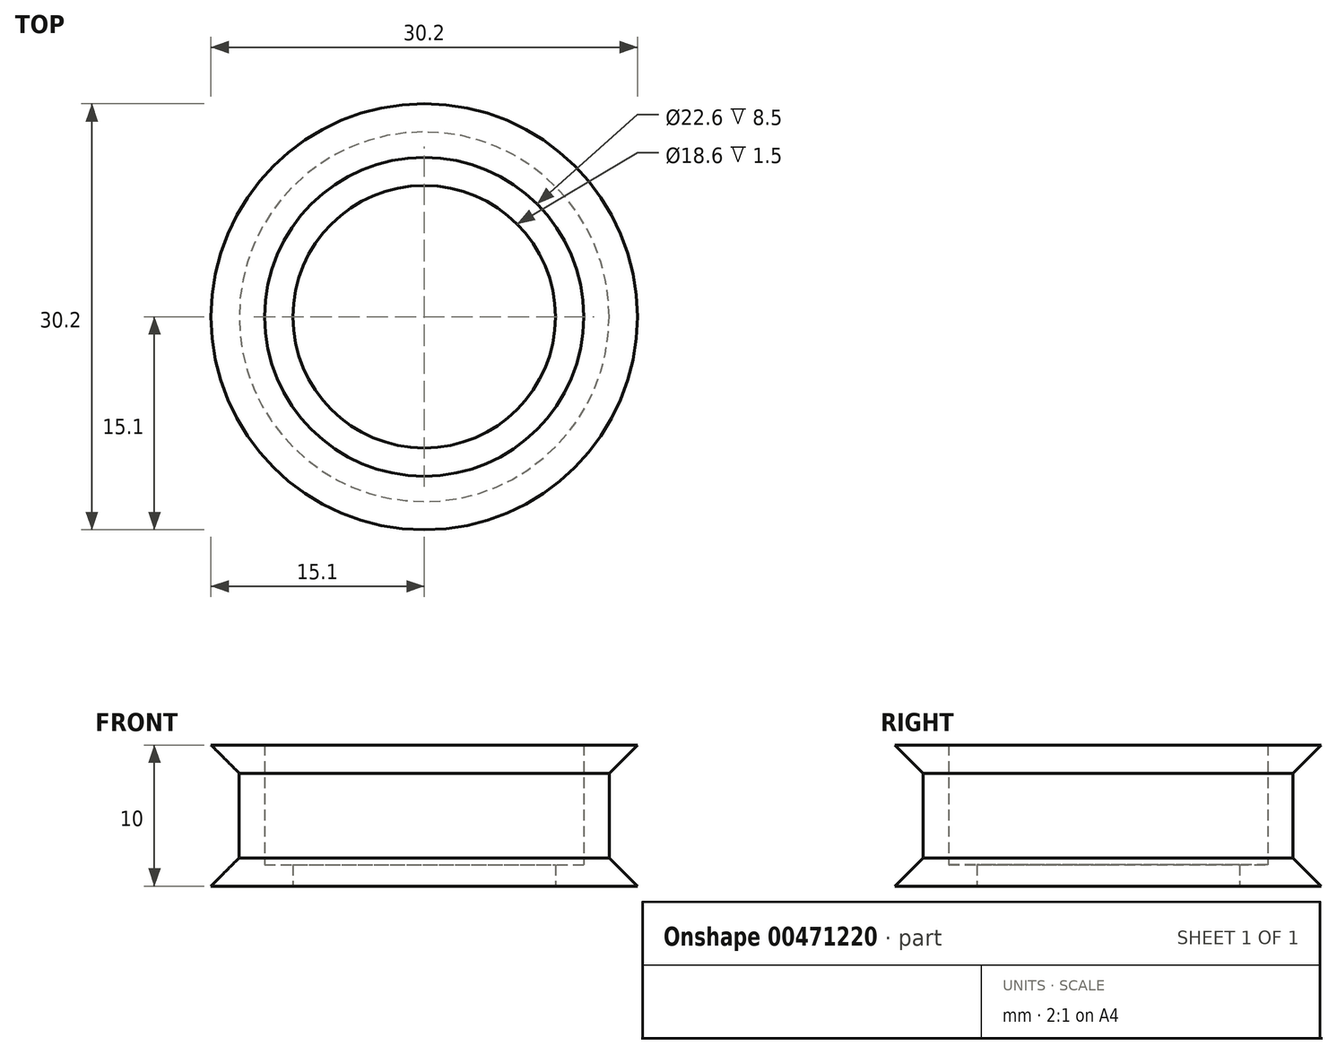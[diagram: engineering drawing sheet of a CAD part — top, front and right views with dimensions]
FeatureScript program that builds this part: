
annotation { "Feature Type Name" : "Feature", "Feature Type Description" : "" }
export const myFeature = defineFeature(function(context is Context, id is Id, definition is map)
    precondition{}
    {
        {
            var Q0;
            Q0=qCreatedBy(makeId("Front.planeOp"),FACE);
            var sketch = newSketch(context, id + "F0", { "sketchPlane" : qUnion([Q0])});
            skLineSegment(sketch, "E0", {"start": v(11.3, 4.8) * mm, "end": v(15.1, 4.8) * mm});
            skLineSegment(sketch, "E1", {"start": v(15.1, 4.8) * mm, "end": v(13.1, 2.8) * mm});
            skLineSegment(sketch, "E2", {"start": v(13.1, 2.8) * mm, "end": v(13.1, -3.2) * mm});
            skLineSegment(sketch, "E3", {"start": v(13.1, -3.2) * mm, "end": v(15.1, -5.2) * mm});
            skLineSegment(sketch, "E4", {"start": v(15.1, -5.2) * mm, "end": v(11.3, -5.2) * mm});
            skLineSegment(sketch, "E5", {"start": v(11.3, -5.2) * mm, "end": v(11.3, 4.8) * mm});
            skLineSegment(sketch, "E6", {"start": v(0, -3.77) * mm, "end": v(0, 4.95) * mm, "construction": true});
            skLineSegment(sketch, "E7.bottom", {"start": v(11.3, -5.2) * mm, "end": v(9.3, -5.2) * mm});
            skLineSegment(sketch, "E7.top", {"start": v(11.3, -3.7) * mm, "end": v(9.3, -3.7) * mm});
            skLineSegment(sketch, "E7.left", {"start": v(11.3, -5.2) * mm, "end": v(11.3, -3.7) * mm});
            skLineSegment(sketch, "E7.right", {"start": v(9.3, -5.2) * mm, "end": v(9.3, -3.7) * mm});
            skSolve(sketch);
        }
        {
            var Q0;
            Q0=qSketchRegion(id+"F0",true);
            var Q1;
            Q1=sQuery(id+"F0.wireOp",EDGE,"E6");
            revolve(context, id + "F1", {"entities" : qUnion([Q0]), "axis" : qUnion([Q1]), "revolveType" : RevolveType.FULL});
        }
    });
